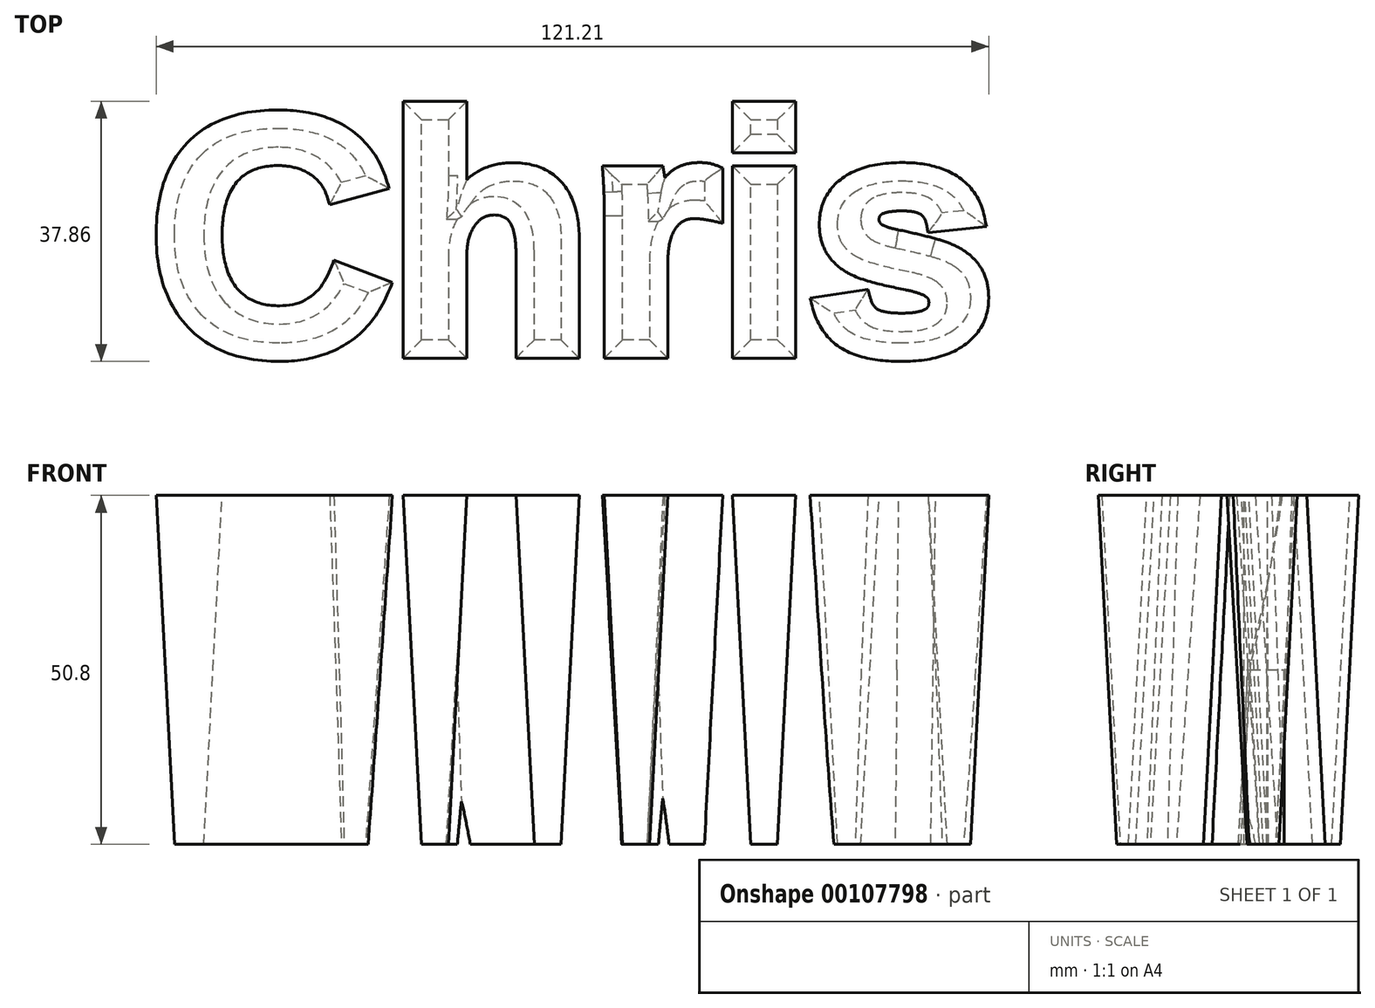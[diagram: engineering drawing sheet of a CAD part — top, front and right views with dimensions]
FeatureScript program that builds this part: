
annotation { "Feature Type Name" : "Feature", "Feature Type Description" : "" }
export const myFeature = defineFeature(function(context is Context, id is Id, definition is map)
    precondition{}
    {
        {
            var Q0;
            Q0=qCreatedBy(makeId("Top.planeOp"),FACE);
            var sketch = newSketch(context, id + "F0", { "sketchPlane" : qUnion([Q0])});
            skText(sketch, "E0", { "text": "Chris", "fontName": "Arimo-Bold.ttf"});
            const initialGuessF0  = {"E0": [-0.13391, -0.00908, 1, 0, 0.0345]};
            skSetInitialGuess(sketch, initialGuessF0);
            skSolve(sketch);
        }
        {
            var Q0;
            Q0=qCreatedBy(makeId("Right.planeOp"),FACE);
            cPlane(context, id + "F1", {"entities" : qUnion([Q0]), "cplaneType" : CPlaneType.OFFSET, "offset" : 63.5 * mm, "oppositeDirection" : true, "width" : 152.4 * mm, "height" : 152.4 * mm});
        }
        {
            var Q0;
            Q0=makeQuery(id+"F0.imprint","IMPRINT",FACE,{"disambiguationData":[TD([[makeQuery(id+"F0.imprint","IMPRINT",EDGE,{"derivedFrom":sQuery(id+"F0.wireOp",EDGE,"E0.sketch_text.stroke-0")}),-1.0]])]});
            var Q1;
            Q1 = qSketchRegion(id + "F0", true);
            extrude(context, id + "F2", {"entities" : qUnion([Q0, Q1]), "depth" : 25.4 * mm, "hasDraft" : true, "draftAngle" : 3 * degree, "hasSecondDirection" : true, "secondDirectionOppositeDirection" : true, "secondDirectionDepth" : 25.4 * mm, "hasSecondDirectionDraft" : true, "secondDirectionDraftAngle" : 3 * degree, "secondDirectionDraftPullDirection" : true});
        }
    });
